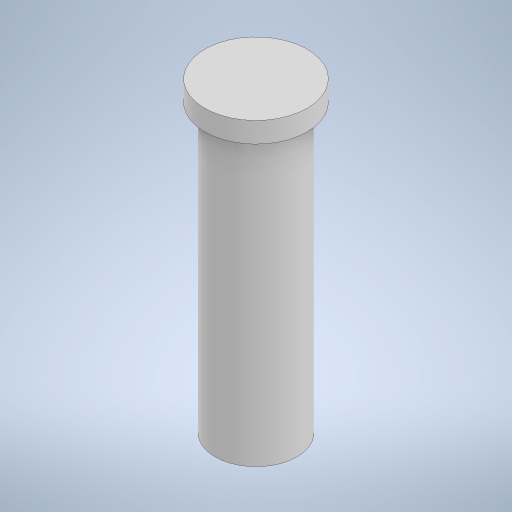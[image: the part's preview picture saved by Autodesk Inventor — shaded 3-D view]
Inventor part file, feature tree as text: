
AUTODESK INVENTOR PART (.ipt)
format: ipt  version: 2024 (Build 280153000, 153)  size: 216,576 bytes
history: native  units: mm
features: revolve x1, sketch x1
ambient origin geometry x8: Origin, YZ Plane, XZ Plane, XY Plane, X Axis, Y Axis, Z Axis, Center Point
bodies: Solid1 (feature_tree)
feature tree (2):
  revolve  "Revolution1"  [1 undecoded]
  sketch  "Sketch1"  dims[d0=4.0mm d1=28.0mm d2=1.0mm d3=2.0mm d4=5.0mm d5=90.0deg]
note: 1 required parameter value undecoded (feature->parameter linkage not recoverable at this tier; creation-order binding heuristic only, values carry confidence <= 0.55)
